# Revit family: Балконный блок с одностворчатым окном справа
name_source: partatom
category: Окна
revit_build: Autodesk Revit 2016 (Build: 20160314_0715(x64)
units: mm (PartAtom-declared; Revit-internal decimal feet)

## family parameters
Всегда вертикально = Да
Заголовок OmniClass = Doors
Номер OmniClass = 23.30.10.00
Общий = Нет
Основа = Стена
При загрузке вырезать с полостями = Нет
Точка расчета площади = Нет

## types (3) — shared parameters
ADSK_URL документации изделия = http://store.brusbox.ru
ADSK_URL страницы изделия = https://brusbox.ru
ADSK_Версия Revit = Autodesk Revit 2016
ADSK_Единица измерения = шт
ADSK_Завод-изготовитель = ООО "БРУСБОКС"
ADSK_Количество = 1
BL_BIM library = https://bimlib.ru
Rед = 1.0000 (м²·K)/Вт
URL = https://brusbox.ru
λ_КраевойЗоныСтеклопакета = 0.0600 (м²·K)/Вт
Аналитическая конструкция = <Нет>
Замыкание стены = По основе
ЗубСтворки_Высота = 20 мм
Изготовитель = ООО ''БРУСБОКС''
КлассПожарнойОпасности = КМ3
Отлив_Материал = <По категории>
Подоконник_Материал = <По категории>
Профиль_Материал = <По категории>
ПрофильПодставочный_Ширина = 28 мм
РасчетноеЗначениеВетровойНагрузки = 400
Створка_ВысотаПрофиля = 60 мм
Стеклопакет_Материал = Стекло
Сэндвич_Материал = <По категории>
Сэндвич_Толщина = 32 мм
ТехническиеУсловия_или_ГОСТ = ГОСТ 30673-2013, ГОСТ-24866-2014, ГОСТ-30674-99, ГОСТ 30971-2012
zero-valued in all types: Высота, Выступ каркаса внут., Выступ каркаса нар., Примерная высота, Примерная ширина, Толщина, Ширина, Ширина каркаса

## per-type parameters (varying)
| type | ADSK_Наименование краткое | Rпрофиля | Rстеклопакета | АртикулИмпоста_АрмированияИмпоста | АртикулРамы_АрмированияРамы | АртикулСтворки_АрмированияСтворки | ЗубСтворки_Ширина | Импост_ВысотаПрофиля | КлассСопротивленияТеплопередаче | Наименование | ПрофильПодставочный_Артикул | ПрофильПодставочный_Высота | Рама_ВысотаПрофиля | Рама_ШиринаПрофиля | Смещение | Створка_ШиринаПрофиля | Стеклопакет_Толщина | Стеклопакет_Формула |
| BRUSBOX ACLASS | Балкон. блок с 1-ств. окном справа BRUSBOX ACLASS | 0.7300 (м²·K)/Вт | 0.7500 (м²·K)/Вт | 11103078/40108020 | 11101060/40108020 | 11102060/40108028 | 14 мм | 78 мм | Б1 | Балконный блок с одностворчатым окном справа BRUSBOX ACLASS | 40106030 | 30 мм | 60 мм | 60 мм | 18 мм | 60 мм | 32 мм | 4-10-4-10-4И |
| BRUSBOX SUPER AERO | Балкон. блок с 1-ств. окном справа BRUSBOX SUPER AERO | 0.8800 (м²·K)/Вт | 0.7500 (м²·K)/Вт | 10603078/40108020 | 10601060/40108020 | 10602060/40108028 | 16 мм | 78 мм | А2 | Балконный блок с одностворчатым окном справа BRUSBOX SUPER AERO | 40006033 | 25 мм | 60 мм | 70 мм | 20 мм | 70 мм | 40 мм | 4-14-4-14-4И |
| BRUSBOX 70-6 | Балкон. блок с 1-ств. окном справа BRUSBOX 70-6 | 0.9300 (м²·K)/Вт | 0.9300 (м²·K)/Вт | 10403086/40108028 | 10401064/40108020 | 10402060/40108028 | 16 мм | 86 мм | А1 | Балконный блок с одностворчатым окном справа BRUSBOX 70-6 | 40106030 | 30 мм | 64 мм | 70 мм | 20 мм | 70 мм | 40 мм | 4И-14-4-14-4И |

note: column(s) folded — value = type name in every type: ПрофильнаяСистема_Наименование

## geometry (parser evidence)
native form markers: Blend x10
no freeform markers — native parametric forms only
